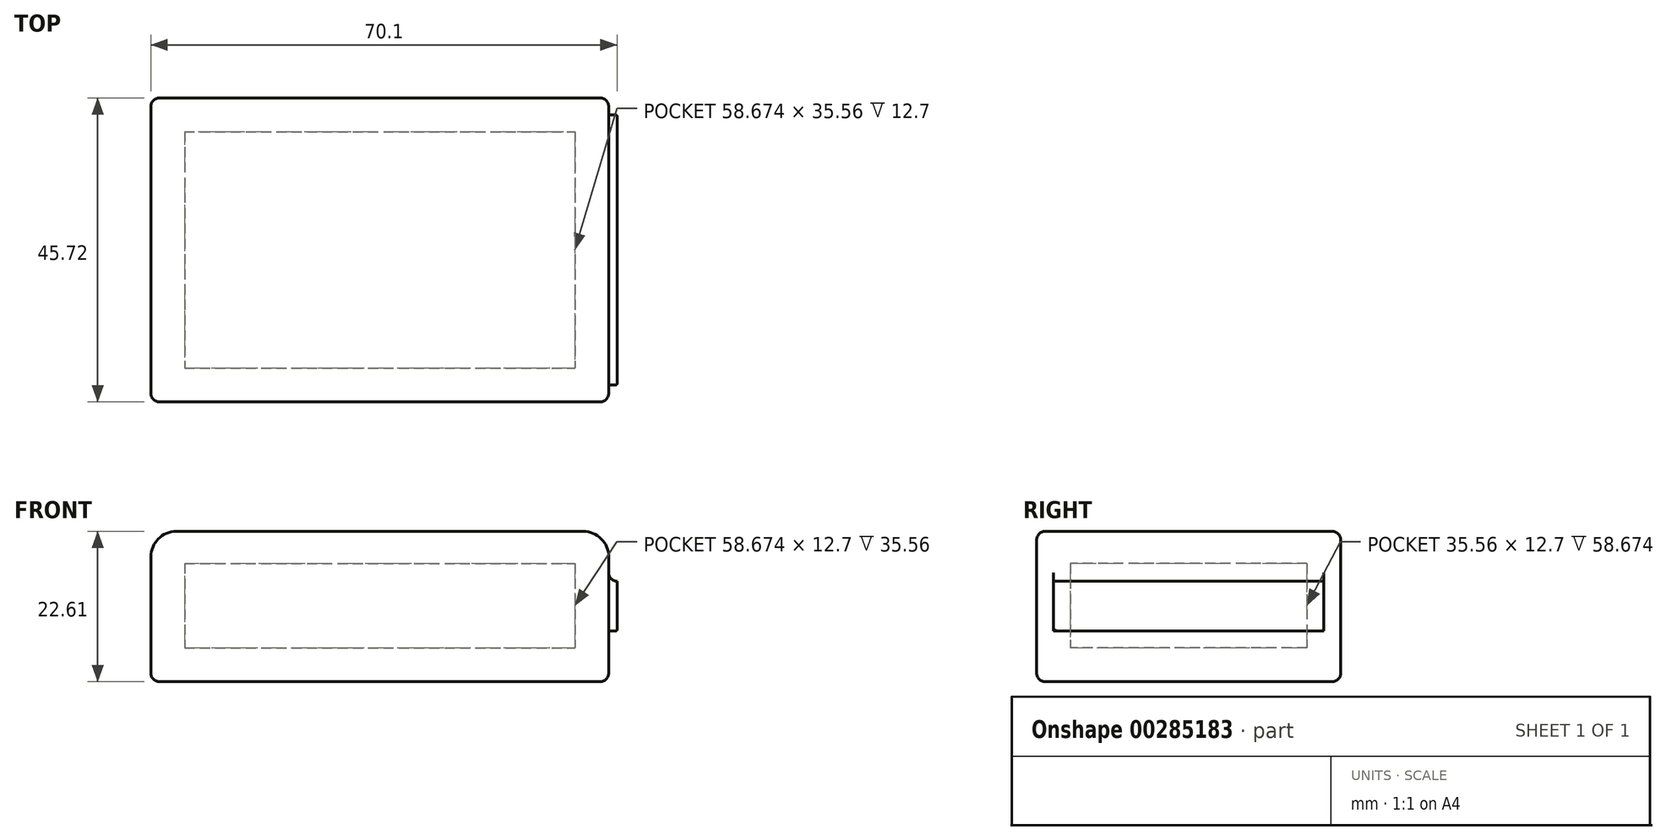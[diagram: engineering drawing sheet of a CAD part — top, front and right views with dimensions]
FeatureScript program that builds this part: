
annotation { "Feature Type Name" : "Feature", "Feature Type Description" : "" }
export const myFeature = defineFeature(function(context is Context, id is Id, definition is map)
    precondition{}
    {
        {
            var Q0;
            Q0=qCreatedBy(makeId("Top.planeOp"),FACE);
            var sketch = newSketch(context, id + "F0", { "sketchPlane" : qUnion([Q0])});
            skLineSegment(sketch, "E0.bottom", {"start": v(0, 0) * mm, "end": v(68.83, 0) * mm});
            skLineSegment(sketch, "E0.top", {"start": v(0, 45.72) * mm, "end": v(68.83, 45.72) * mm});
            skLineSegment(sketch, "E0.left", {"start": v(0, 0) * mm, "end": v(0, 45.72) * mm});
            skLineSegment(sketch, "E0.right", {"start": v(68.83, 0) * mm, "end": v(68.83, 45.72) * mm});
            skSolve(sketch);
        }
        {
            var Q0;
            Q0 = qSketchRegion(id + "F0", true);
            extrude(context, id + "F1", {"entities" : qUnion([Q0]), "depth" : 5.08 * mm});
        }
        {
            var Q0;
            Q0=makeQuery(id+"F1.opExtrude","CAP_FACE",FACE,{"disambiguationData":[OSD([sQuery(id+"F0.wireOp",EDGE,"E0.bottom"),sQuery(id+"F0.wireOp",EDGE,"E0.top"),sQuery(id+"F0.wireOp",EDGE,"E0.left"),sQuery(id+"F0.wireOp",EDGE,"E0.right")])],"isStart":false});
            var sketch = newSketch(context, id + "F2", { "sketchPlane" : qUnion([Q0])});
            skLineSegment(sketch, "E1.bottom", {"start": v(0, 45.72) * mm, "end": v(68.83, 45.72) * mm});
            skLineSegment(sketch, "E1.top", {"start": v(0, 0) * mm, "end": v(68.83, 0) * mm});
            skLineSegment(sketch, "E1.left", {"start": v(0, 45.72) * mm, "end": v(0, 0) * mm});
            skLineSegment(sketch, "E1.right", {"start": v(68.83, 45.72) * mm, "end": v(68.83, 0) * mm});
            skLineSegment(sketch, "E2.0", {"start": v(5.08, 40.64) * mm, "end": v(63.75, 40.64) * mm});
            skLineSegment(sketch, "E2.1", {"start": v(5.08, 40.64) * mm, "end": v(5.08, 5.08) * mm});
            skLineSegment(sketch, "E2.2", {"start": v(5.08, 5.08) * mm, "end": v(63.75, 5.08) * mm});
            skLineSegment(sketch, "E2.3", {"start": v(63.75, 40.64) * mm, "end": v(63.75, 5.08) * mm});
            skSolve(sketch);
        }
        {
            var Q0;
            Q0=makeQuery(id+"F2.imprint","IMPRINT",FACE,{"disambiguationData":[TD([[makeQuery(id+"F2.imprint","IMPRINT",EDGE,{"derivedFrom":sQuery(id+"F2.wireOp",EDGE,"E1.bottom")}),-1.0]])]});
            extrude(context, id + "F3", {"entities" : qUnion([Q0]), "operationType" : NewBodyOperationType.ADD, "depth" : 6.35 * mm});
        }
        {
            var Q0;
            Q0=makeQuery(id+"F3.opExtrude","CAP_FACE",FACE,{"disambiguationData":[OSD([sQuery(id+"F2.wireOp",EDGE,"E1.bottom"),sQuery(id+"F2.wireOp",EDGE,"E1.top"),sQuery(id+"F2.wireOp",EDGE,"E1.left"),sQuery(id+"F2.wireOp",EDGE,"E1.right"),sQuery(id+"F2.wireOp",EDGE,"E2.0"),sQuery(id+"F2.wireOp",EDGE,"E2.1"),sQuery(id+"F2.wireOp",EDGE,"E2.2"),sQuery(id+"F2.wireOp",EDGE,"E2.3")])],"isStart":false});
            var sketch = newSketch(context, id + "F4", { "sketchPlane" : qUnion([Q0])});
            skLineSegment(sketch, "E3.bottom", {"start": v(0, 45.72) * mm, "end": v(68.83, 45.72) * mm});
            skLineSegment(sketch, "E3.top", {"start": v(0, 0) * mm, "end": v(68.83, 0) * mm});
            skLineSegment(sketch, "E3.left", {"start": v(0, 45.72) * mm, "end": v(0, 0) * mm});
            skLineSegment(sketch, "E3.right", {"start": v(68.83, 45.72) * mm, "end": v(68.83, 0) * mm});
            skLineSegment(sketch, "E4.bottom", {"start": v(63.75, 40.64) * mm, "end": v(5.08, 40.64) * mm});
            skLineSegment(sketch, "E4.top", {"start": v(63.75, 5.08) * mm, "end": v(5.08, 5.08) * mm});
            skLineSegment(sketch, "E4.left", {"start": v(63.75, 40.64) * mm, "end": v(63.75, 5.08) * mm});
            skLineSegment(sketch, "E4.right", {"start": v(5.08, 40.64) * mm, "end": v(5.08, 5.08) * mm});
            skSolve(sketch);
        }
        {
            var Q0;
            Q0 = qSketchRegion(id + "F4", true);
            extrude(context, id + "F5", {"entities" : qUnion([Q0]), "depth" : 6.35 * mm});
        }
        {
            var Q0;
            Q0=makeQuery(id+"F5.opExtrude","CAP_FACE",FACE,{"disambiguationData":[OSD([sQuery(id+"F4.wireOp",EDGE,"E3.bottom"),sQuery(id+"F4.wireOp",EDGE,"E3.top"),sQuery(id+"F4.wireOp",EDGE,"E3.left"),sQuery(id+"F4.wireOp",EDGE,"E3.right"),sQuery(id+"F4.wireOp",EDGE,"E4.bottom"),sQuery(id+"F4.wireOp",EDGE,"E4.top"),sQuery(id+"F4.wireOp",EDGE,"E4.left"),sQuery(id+"F4.wireOp",EDGE,"E4.right")])],"isStart":false});
            var sketch = newSketch(context, id + "F6", { "sketchPlane" : qUnion([Q0])});
            skLineSegment(sketch, "E5.bottom", {"start": v(0, 45.72) * mm, "end": v(68.83, 45.72) * mm});
            skLineSegment(sketch, "E5.top", {"start": v(0, 0) * mm, "end": v(68.83, 0) * mm});
            skLineSegment(sketch, "E5.left", {"start": v(0, 45.72) * mm, "end": v(0, 0) * mm});
            skLineSegment(sketch, "E5.right", {"start": v(68.83, 45.72) * mm, "end": v(68.83, 0) * mm});
            skSolve(sketch);
        }
        {
            var Q0;
            Q0 = qSketchRegion(id + "F6", true);
            extrude(context, id + "F7", {"entities" : qUnion([Q0]), "operationType" : NewBodyOperationType.ADD, "depth" : 4.83 * mm});
        }
        {
            var Q0;
            Q0=makeQuery(id+"F7.boolean.opBoolean","MERGE",FACE,{"derivedFrom":[makeQuery(id+"F5.opExtrude","SWEPT_FACE",FACE,{"disambiguationData":[OSD([sQuery(id+"F4.wireOp",EDGE,"E3.right")])]}),makeQuery(id+"F7.opExtrude","SWEPT_FACE",FACE,{"disambiguationData":[OSD([sQuery(id+"F6.wireOp",EDGE,"E5.right")])]})]});
            var sketch = newSketch(context, id + "F8", { "sketchPlane" : qUnion([Q0])});
            skLineSegment(sketch, "E6.top", {"start": v(2.54, 7.62) * mm, "end": v(43.18, 7.62) * mm});
            skLineSegment(sketch, "E6.left", {"start": v(2.54, 22.6) * mm, "end": v(2.54, 7.62) * mm});
            skLineSegment(sketch, "E6.right", {"start": v(43.18, 22.6) * mm, "end": v(43.18, 7.62) * mm});
            skLineSegment(sketch, "E7", {"start": v(2.54, 15.11) * mm, "end": v(43.18, 15.11) * mm});
            skSolve(sketch);
        }
        {
            var Q0;
            {var subQ0=sQuery(id+"F8.wireOp",EDGE,"E6.bottom");Q0=makeQuery(id+"F8.imprint","IMPRINT",FACE,{"disambiguationData":[TD([[makeQuery(id+"F8.imprint","IMPRINT",EDGE,{"derivedFrom":subQ0}),-1.0]])]});}
            var Q1;
            {var subQ0=sQuery(id+"F8.wireOp",EDGE,"E6.top");Q1=makeQuery(id+"F8.imprint","IMPRINT",FACE,{"disambiguationData":[TD([[makeQuery(id+"F8.imprint","IMPRINT",EDGE,{"derivedFrom":subQ0}),1.0]])]});}
            var Q2;
            {var subQ0=sQuery(id+"F8.wireOp",EDGE,"E7");Q2=makeQuery(id+"F8.imprint","IMPRINT",FACE,{"disambiguationData":[TD([[makeQuery(id+"F8.imprint","IMPRINT",EDGE,{"derivedFrom":subQ0}),-1.0]])]});}
            extrude(context, id + "F9", {"entities" : qUnion([Q0, Q1, Q2]), "operationType" : NewBodyOperationType.ADD, "depth" : 1.27 * mm});
        }
        {
            var Q0;
            Q0=makeQuery(id+"F7.opExtrude","CAP_EDGE",EDGE,{"disambiguationData":[OSD([sQuery(id+"F6.wireOp",EDGE,"E5.right")])],"isStart":false});
            var Q1;
            Q1=makeQuery(id+"F7.opExtrude","CAP_EDGE",EDGE,{"disambiguationData":[OSD([sQuery(id+"F6.wireOp",EDGE,"E5.left")])],"isStart":false});
            fillet(context, id + "F10", {"entities" : qUnion([Q0, Q1]), "radius" : 3.8 * mm, "tangentPropagation" : true, "allowEdgeOverflow" : false});
        }
        {
            var Q0;
            Q0=makeQuery(id+"F7.opExtrude","CAP_EDGE",EDGE,{"disambiguationData":[OSD([sQuery(id+"F6.wireOp",EDGE,"E5.top")])],"isStart":false});
            var Q1;
            Q1=makeQuery(id+"F7.opExtrude","CAP_EDGE",EDGE,{"disambiguationData":[OSD([sQuery(id+"F6.wireOp",EDGE,"E5.bottom")])],"isStart":false});
            var Q2;
            Q2=makeQuery(id+"F9.opExtrude","CAP_EDGE",EDGE,{"disambiguationData":[OSD([sQuery(id+"F8.wireOp",EDGE,"E7")])],"isStart":true});
            var Q3;
            {var subQ0=sQuery(id+"F8.wireOp",EDGE,"E6.left");Q3=makeQuery(id+"F9.boolean.opBoolean","SPLIT",EDGE,{"disambiguationData":[topologyDisambiguationEdgeConnected([makeQuery(id+"F5.opExtrude","SWEPT_FACE",FACE,{"disambiguationData":[OSD([sQuery(id+"F4.wireOp",EDGE,"E3.right")])]})])],"derivedFrom":makeQuery(id+"F9.opExtrude","CAP_EDGE",EDGE,{"disambiguationData":[OSD([subQ0])],"isStart":true})});}
            var Q4;
            {var subQ0=sQuery(id+"F8.wireOp",EDGE,"E6.right");Q4=makeQuery(id+"F9.boolean.opBoolean","SPLIT",EDGE,{"disambiguationData":[topologyDisambiguationEdgeConnected([makeQuery(id+"F5.opExtrude","SWEPT_FACE",FACE,{"disambiguationData":[OSD([sQuery(id+"F4.wireOp",EDGE,"E3.right")])]})])],"derivedFrom":makeQuery(id+"F9.opExtrude","CAP_EDGE",EDGE,{"disambiguationData":[OSD([subQ0])],"isStart":true})});}
            var Q5;
            Q5=makeQuery(id+"F3.boolean.opBoolean","MERGE",EDGE,{"derivedFrom":[makeQuery(id+"F1.opExtrude","SWEPT_EDGE",EDGE,{"disambiguationData":[OSD([sQuery(id+"F0.wireOp",EDGE,"E0.bottom"),sQuery(id+"F0.wireOp",EDGE,"E0.right")])]}),makeQuery(id+"F3.opExtrude","SWEPT_EDGE",EDGE,{"disambiguationData":[OSD([sQuery(id+"F2.wireOp",EDGE,"E1.top"),sQuery(id+"F2.wireOp",EDGE,"E1.right")])]})]});
            var Q6;
            Q6=makeQuery(id+"F3.boolean.opBoolean","MERGE",EDGE,{"derivedFrom":[makeQuery(id+"F1.opExtrude","SWEPT_EDGE",EDGE,{"disambiguationData":[OSD([sQuery(id+"F0.wireOp",EDGE,"E0.bottom"),sQuery(id+"F0.wireOp",EDGE,"E0.left")])]}),makeQuery(id+"F3.opExtrude","SWEPT_EDGE",EDGE,{"disambiguationData":[OSD([sQuery(id+"F2.wireOp",EDGE,"E1.top"),sQuery(id+"F2.wireOp",EDGE,"E1.left")])]})]});
            var Q7;
            Q7=makeQuery(id+"F1.opExtrude","CAP_EDGE",EDGE,{"disambiguationData":[OSD([sQuery(id+"F0.wireOp",EDGE,"E0.bottom")])],"isStart":true});
            var Q8;
            Q8=makeQuery(id+"F1.opExtrude","CAP_EDGE",EDGE,{"disambiguationData":[OSD([sQuery(id+"F0.wireOp",EDGE,"E0.right")])],"isStart":true});
            var Q9;
            Q9=makeQuery(id+"F3.boolean.opBoolean","MERGE",EDGE,{"derivedFrom":[makeQuery(id+"F1.opExtrude","SWEPT_EDGE",EDGE,{"disambiguationData":[OSD([sQuery(id+"F0.wireOp",EDGE,"E0.top"),sQuery(id+"F0.wireOp",EDGE,"E0.right")])]}),makeQuery(id+"F3.opExtrude","SWEPT_EDGE",EDGE,{"disambiguationData":[OSD([sQuery(id+"F2.wireOp",EDGE,"E1.bottom"),sQuery(id+"F2.wireOp",EDGE,"E1.right")])]})]});
            var Q10;
            Q10=makeQuery(id+"F1.opExtrude","CAP_EDGE",EDGE,{"disambiguationData":[OSD([sQuery(id+"F0.wireOp",EDGE,"E0.top")])],"isStart":true});
            var Q11;
            Q11=makeQuery(id+"F3.boolean.opBoolean","MERGE",EDGE,{"derivedFrom":[makeQuery(id+"F1.opExtrude","SWEPT_EDGE",EDGE,{"disambiguationData":[OSD([sQuery(id+"F0.wireOp",EDGE,"E0.top"),sQuery(id+"F0.wireOp",EDGE,"E0.left")])]}),makeQuery(id+"F3.opExtrude","SWEPT_EDGE",EDGE,{"disambiguationData":[OSD([sQuery(id+"F2.wireOp",EDGE,"E1.bottom"),sQuery(id+"F2.wireOp",EDGE,"E1.left")])]})]});
            var Q12;
            Q12=makeQuery(id+"F1.opExtrude","CAP_EDGE",EDGE,{"disambiguationData":[OSD([sQuery(id+"F0.wireOp",EDGE,"E0.left")])],"isStart":true});
            fillet(context, id + "F11", {"entities" : qUnion([Q0, Q1, Q2, Q3, Q4, Q5, Q6, Q7, Q8, Q9, Q10, Q11, Q12]), "radius" : 1.27 * mm, "tangentPropagation" : true, "allowEdgeOverflow" : false});
        }
        {
            var Q0;
            Q0=makeQuery(id+"F9.opExtrude","CAP_EDGE",EDGE,{"disambiguationData":[OSD([sQuery(id+"F8.wireOp",EDGE,"E6.left")])],"isStart":false});
            var Q1;
            Q1=makeQuery(id+"F9.opExtrude","CAP_EDGE",EDGE,{"disambiguationData":[OSD([sQuery(id+"F8.wireOp",EDGE,"E6.top")])],"isStart":false});
            var Q2;
            Q2=makeQuery(id+"F9.opExtrude","CAP_EDGE",EDGE,{"disambiguationData":[OSD([sQuery(id+"F8.wireOp",EDGE,"E6.right")])],"isStart":false});
            fillet(context, id + "F12", {"entities" : qUnion([Q0, Q1, Q2]), "radius" : 0.25 * mm, "tangentPropagation" : true, "allowEdgeOverflow" : false});
        }
    });
